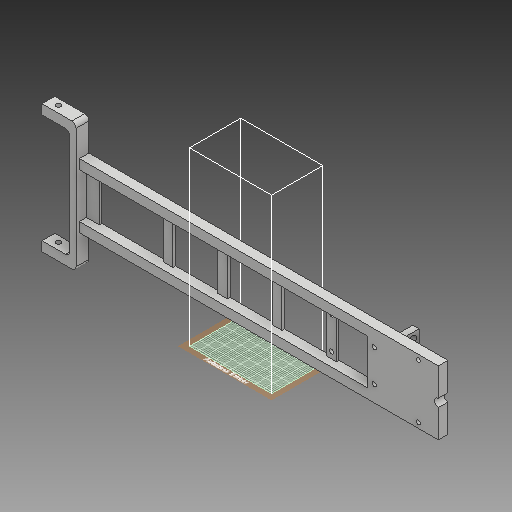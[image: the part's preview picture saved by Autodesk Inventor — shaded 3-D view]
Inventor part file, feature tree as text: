
AUTODESK INVENTOR PART (.ipt)
format: ipt  version: 2018 (Build 220112000, 112)  size: 911,360 bytes
history: native  units: mm
features: sketch x63, extrude x48, fillet x13, hole x6, plane x1
ambient origin geometry x8: Origin, YZ Plane, XZ Plane, XY Plane, X Axis, Y Axis, Z Axis, Center Point
bodies: Solid1 (feature_tree)
feature tree (131):
  extrude  "Extrusion1"  Depth=50.0mm
  hole  "Hole1"  [1 undecoded]
  hole  "Hole2"  [1 undecoded]
  extrude  "Extrusion2"  Depth=25.0mm
  extrude  "Extrusion3"  Depth=25.0mm
  extrude  "Extrusion4"  Depth=5.0mm
  sketch  "Sketch7"  dims[d25=10.0mm d26=5.0mm]
  extrude  "Extrusion5"  Depth=5.0mm
  extrude  "Extrusion6"  Depth=35.0mm
  extrude  "Extrusion7"  Depth=35.0mm
  extrude  "Extrusion8"  Depth=35.0mm
  extrude  "Extrusion9"  Depth=2.0mm TaperAngle=0.0deg
  extrude  "Extrusion10"  Depth=7.5mm TaperAngle=0.0deg
  extrude  "Extrusion11"  Depth=10.0mm
  extrude  "Extrusion12"  Depth=7.5mm
  fillet  "Fillet1"  Radius=7.5mm
  fillet  "Fillet2"  Radius=25.0mm
  fillet  "Fillet3"  Radius=3.0mm
  fillet  "Fillet4"  Radius=3.2mm
  fillet  "Fillet5"  Radius=2.1mm
  fillet  "Fillet6"  Radius=5.5mm
  extrude  "Extrusion13"  Depth=92.5mm TaperAngle=0.0deg
  sketch  "Sketch17"  dims[d58=4.25mm d59=241.0mm d60=0.0mm]
  hole  "Hole3"  [1 undecoded]
  hole  "Hole4"  [1 undecoded]
  extrude  "Extrusion14"  Depth=5.0mm
  extrude  "Extrusion15"  Depth=2.5mm TaperAngle=0.0deg
  extrude  "Extrusion16"  Depth=30.0mm
  extrude  "Extrusion17"  Depth=2.5mm
  extrude  "Extrusion18"  Depth=14.55mm TaperAngle=0.0deg
  extrude  "Extrusion19"  Depth=0.1mm
  extrude  "Extrusion20"  Depth=3.25mm
  extrude  "Extrusion21"  Depth=3.25mm
  hole  "Hole5"  [1 undecoded]
  extrude  "Extrusion22"  Depth=2.0mm
  extrude  "Extrusion23"  Depth=15.0mm
  extrude  "Extrusion24"  Depth=10.0mm TaperAngle=0.0deg
  hole  "Hole6"  [1 undecoded]
  extrude  "Extrusion25"  Depth=100.0mm TaperAngle=0.0deg
  extrude  "Extrusion26"  Depth=2.0mm TaperAngle=0.0deg
  sketch  "Sketch35"  dims[d116=3.3mm d117=3.3mm]
  plane  "Work Plane1"
  sketch  "Sketch36"  dims[d118=3.3mm d119=3.3mm d120=2.0mm d121=0.0mm]
  extrude  "Extrusion27"  Depth=3.3mm
  extrude  "Extrusion28"  Depth=2.0mm
  fillet  "Fillet7"  Radius=2.0mm
  extrude  "Extrusion29"  Depth=8.0mm
  extrude  "Extrusion30"  Depth=21.0mm
  extrude  "Extrusion31"  Depth=8.5mm
  extrude  "Extrusion32"  Depth=3.5mm
  sketch  "Sketch43"  dims[d142=10.0mm d143=0.0mm d144=7.5mm d145=0.0mm]
  fillet  "Fillet8"  Radius=3.3mm
  extrude  "Extrusion33"  Depth=3.3mm
  extrude  "Extrusion34"  Depth=7.5mm TaperAngle=0.0deg
  extrude  "Extrusion35"  Depth=15.0mm
  extrude  "Extrusion36"  Depth=100.0mm TaperAngle=0.0deg
  extrude  "Extrusion37"  Depth=5.0mm
  fillet  "Fillet9"  Radius=5.0mm
  fillet  "Fillet10"  Radius=37.5mm
  fillet  "Fillet11"  Radius=1.1mm
  fillet  "Fillet12"  Radius=37.5mm
  sketch  "Sketch49"  dims[d170=5.5mm d171=0.0mm d172=10.0mm d173=0.0mm]
  extrude  "Extrusion38"  Depth=3.0mm
  extrude  "Extrusion39"  Depth=10.0mm TaperAngle=0.0deg
  extrude  "Extrusion40"  Depth=74.724mm
  fillet  "Fillet13"  Radius=85.515mm
  extrude  "Extrusion41"  Depth=5.0mm
  extrude  "Extrusion42"  Depth=5.0mm
  sketch  "Sketch55"  dims[d186=10.0mm d187=2.0mm d188=0.0mm]
  extrude  "Extrusion43"  Depth=5.0mm
  extrude  "Extrusion44"  Depth=2.0mm TaperAngle=0.0deg
  sketch  "Sketch58"  dims[d195=1.0mm d196=0.0mm d197=20.0mm]
  extrude  "Extrusion45"  Depth=2.0mm TaperAngle=0.0deg
  extrude  "Extrusion46"  Depth=1.0mm TaperAngle=0.0deg
  sketch  "Sketch61"  dims[d201=5.0mm]
  extrude  "Extrusion47"  Depth=10.0mm
  extrude  "Extrusion48"  Depth=20.0mm
  sketch  "Sketch1"  dims[d0=50.0mm d1=50.0mm]
  sketch  "Sketch2"  dims[d2=240.0mm d3=7.5mm]
  sketch  "Sketch3"  dims[d4=7.5mm d5=7.5mm d6=0.0mm]
  sketch  "Sketch4"  dims[d7=6.35mm d8=6.0mm d9=4.0mm d10=2.0mm d11=90.0deg d12=8.0mm d13=20.594885mm d14=25.0mm]
  sketch  "Sketch5"  dims[d15=3.3mm d16=6.0mm d17=4.0mm d18=2.0mm d19=90.0deg d20=8.0mm d21=20.594885mm d22=25.0mm]
  sketch  "Sketch6"  dims[d23=180.0deg d24=5.0mm]
  sketch  "Sketch8"  dims[d27=17.5mm d28=0.0mm d30=35.0mm]
  sketch  "Sketch9"  dims[d31=35.0mm d32=35.0mm]
  sketch  "Sketch10"  dims[d33=35.0mm d34=35.0mm]
  sketch  "Sketch11"  dims[d35=35.0mm d36=2.0mm d37=0.0mm]
  sketch  "Sketch12"  dims[d38=10.0mm d39=7.5mm d40=0.0mm]
  sketch  "Sketch13"  dims[d41=100.0mm d42=10.0mm]
  sketch  "Sketch14"  dims[d43=7.5mm d44=0.0mm d45=7.5mm d46=7.5mm d47=25.0mm d48=0.0mm d49=3.0mm d50=3.2mm d51=2.1mm d52=5.5mm]
  sketch  "Sketch15"  dims[d53=3.3mm d54=92.5mm d55=0.0mm]
  sketch  "Sketch16"  dims[d56=5.5mm d57=3.3mm]
  sketch  "Sketch18"  dims[d61=4.44mm d62=5.0mm]
  sketch  "Sketch19"  dims[d63=2.5mm d64=91.25mm d65=0.0mm]
  sketch  "Sketch20"  dims[d66=30.0mm d67=6.35mm]
  sketch  "Sketch21"  dims[d68=3.8mm d69=0.0mm d70=2.5mm]
  sketch  "Sketch22"  dims[d71=14.55mm d72=0.0mm d73=14.55mm d74=0.0mm]
  sketch  "Sketch23"  dims[d75=0.1mm d76=0.1mm]
  sketch  "Sketch24"  dims[d77=3.25mm d78=3.25mm]
  sketch  "Sketch25"  dims[d79=3.25mm d80=3.25mm]
  sketch  "Sketch26"  dims[d81=35.0mm d82=10.0mm]
  sketch  "Sketch27"  dims[d83=2.0mm d84=0.0mm d85=3.6mm]
  sketch  "Sketch28"  dims[d86=3.6mm]
  sketch  "Sketch29"  dims[d87=3.3mm d88=6.0mm d89=4.0mm d90=2.0mm d91=90.0deg d92=15.0mm d93=20.594885mm]
  sketch  "Sketch30"  dims[d94=3.3mm d95=6.0mm d96=4.0mm d97=2.0mm d98=90.0deg d99=15.0mm d100=20.594885mm d101=6.0mm]
  sketch  "Sketch31"  dims[d102=20.0mm d103=0.0mm d104=10.0mm d105=0.0mm]
  sketch  "Sketch32"  dims[d106=2.0mm d107=0.0mm d108=4.0mm]
  sketch  "Sketch33"  dims[d109=100.0mm d110=0.0mm d111=100.0mm d112=0.0mm]
  sketch  "Sketch34"  dims[d113=5.0mm d114=2.0mm d115=0.0mm]
  sketch  "Sketch37"  dims[d122=5.5mm d123=0.0mm]
  sketch  "Sketch38"  dims[d124=3.3mm d125=6.0mm d126=4.0mm d127=2.0mm d128=90.0deg d129=8.0mm d130=20.594885mm d131=42.0mm]
  sketch  "Sketch39"  dims[d132=17.0mm d133=21.0mm]
  sketch  "Sketch40"  dims[d135=8.5mm d136=15.825mm]
  sketch  "Sketch41"  dims[d137=3.5mm d138=21.0mm d139=3.3mm]
  sketch  "Sketch42"  dims[d140=3.3mm d141=3.3mm]
  sketch  "Sketch44"  dims[d146=100.0mm d147=0.0mm]
  sketch  "Sketch45"  dims[d148=5.0mm d149=6.0mm d150=4.0mm d151=2.0mm d152=90.0deg d153=15.0mm d154=0.0mm d155=3.75mm]
  sketch  "Sketch46"  dims[d156=100.0mm d157=0.0mm d158=100.0mm d159=0.0mm]
  sketch  "Sketch47"  dims[d160=-0.698132mm d161=5.0mm d162=5.0mm d163=37.5mm d164=0.0mm d165=1.1mm d166=37.5mm d167=0.0mm]
  sketch  "Sketch48"  dims[d168=0.2mm d169=3.0mm]
  sketch  "Sketch50"  dims[d174=74.724mm d175=74.724mm d176=85.515mm]
  sketch  "Sketch51"  dims[d177=5.0mm d178=85.515mm]
  sketch  "Sketch52"  dims[d179=5.0mm d180=85.515mm]
  sketch  "Sketch53"  dims[d181=5.0mm d182=85.515mm]
  sketch  "Sketch54"  dims[d183=5.0mm d184=2.0mm d185=0.0mm]
  sketch  "Sketch56"  dims[d189=2.0mm d190=1.0mm d191=0.0mm]
  sketch  "Sketch57"  dims[d192=2.0mm d193=0.0mm d194=10.0mm]
  sketch  "Sketch59"  dims[d198=1.0mm d199=0.0mm]
  sketch  "Sketch60"  dims[d200=7.5mm]
  sketch  "Sketch62"  dims[d202=2.5mm d203=0.0mm]
  sketch  "Sketch63"  dims[d204=3.25mm d205=3.25mm d206=3.25mm d207=3.25mm d208=6.25mm d209=9.58mm d210=250.0mm d211=0.0mm d212=5.25mm d213=4.3mm d214=0.0mm d215=4.3mm d216=0.0mm d217=0.25mm d218=9.7mm d219=100.0mm d220=0.0mm d221=9.8mm d222=4.5mm d223=4.3mm d224=0.0mm d225=9.8mm d226=4.3mm d227=0.0mm d228=10.0mm d229=0.0mm d230=20.0mm d231=10.0mm d232=0.0mm d233=5.0mm d234=5.0mm d235=10.0mm d236=0.0mm d237=3.65mm d238=7.5mm d239=0.0mm d240=7.5mm d241=0.0mm]
note: 6 required parameter values undecoded (feature->parameter linkage not recoverable at this tier; creation-order binding heuristic only, values carry confidence <= 0.55)
